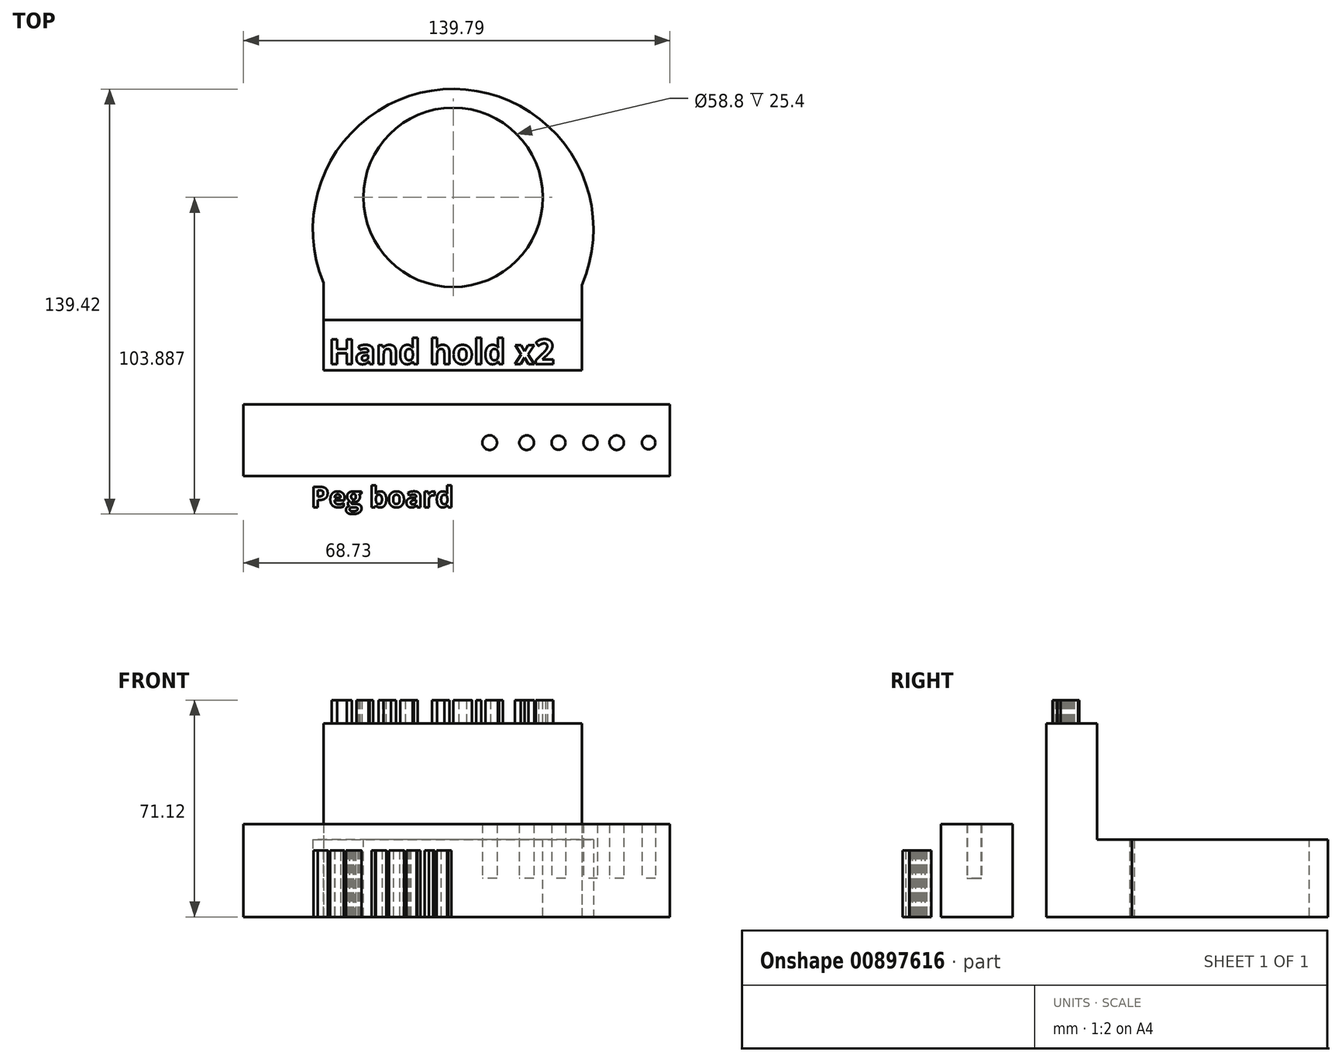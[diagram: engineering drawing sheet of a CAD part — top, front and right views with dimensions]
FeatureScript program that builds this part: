
annotation { "Feature Type Name" : "Feature", "Feature Type Description" : "" }
export const myFeature = defineFeature(function(context is Context, id is Id, definition is map)
    precondition{}
    {
        {
            var Q0;
            Q0=makeQuery(id+"FttHBKo60JJalxO_0.opExtrude","CAP_FACE",FACE,{"disambiguationData":[OSD([sQuery(id+"FFDxyAQckOqJVPz_0.wireOp",EDGE,"cAa8GNnS-9NBn-fBWv-4bFi-mSQCbdk5DH3K"),sQuery(id+"FFDxyAQckOqJVPz_0.wireOp",EDGE,"T3loh2Vf-emFG-5iRX-t4Wo-vKlrmD9mAp1y.bottom"),sQuery(id+"FFDxyAQckOqJVPz_0.wireOp",EDGE,"T3loh2Vf-emFG-5iRX-t4Wo-vKlrmD9mAp1y.top"),sQuery(id+"FFDxyAQckOqJVPz_0.wireOp",EDGE,"T3loh2Vf-emFG-5iRX-t4Wo-vKlrmD9mAp1y.left"),sQuery(id+"FFDxyAQckOqJVPz_0.wireOp",EDGE,"T3loh2Vf-emFG-5iRX-t4Wo-vKlrmD9mAp1y.right"),sQuery(id+"FFDxyAQckOqJVPz_0.wireOp",EDGE,"rmxbEG8E-x7te-680N-vgeH-4cutX0Q7IRPg")])],"isStart":false});
            var sketch = newSketch(context, id + "F0", { "sketchPlane" : qUnion([Q0])});
            skLineSegment(sketch, "E0.bottom", {"start": v(-58.06, -65.24) * mm, "end": v(58.26, -65.24) * mm});
            skLineSegment(sketch, "E0.top", {"start": v(-58.06, -53.15) * mm, "end": v(58.26, -53.15) * mm});
            skLineSegment(sketch, "E0.left", {"start": v(-58.06, -65.24) * mm, "end": v(-58.06, -53.15) * mm});
            skLineSegment(sketch, "E0.right", {"start": v(58.26, -65.24) * mm, "end": v(58.26, -53.15) * mm});
            skSolve(sketch);
        }
        {
            var Q0;
            Q0=qCreatedBy(makeId("Top.planeOp"),FACE);
            var sketch = newSketch(context, id + "F1", { "sketchPlane" : qUnion([Q0])});
            skCircle(sketch, "E1", {"center": v(0, 17.56) * mm, "radius": 46 * mm});
            skLineSegment(sketch, "E2.bottom", {"start": v(-42.51, 0) * mm, "end": v(42.21, 0) * mm});
            skLineSegment(sketch, "E2.top", {"start": v(-42.51, -28.72) * mm, "end": v(42.21, -28.72) * mm});
            skLineSegment(sketch, "E2.left", {"start": v(-42.51, 0) * mm, "end": v(-42.51, -28.72) * mm});
            skLineSegment(sketch, "E2.right", {"start": v(42.21, 0) * mm, "end": v(42.21, -28.72) * mm});
            skSolve(sketch);
        }
        {
            var Q0;
            {var subQ0=sQuery(id+"F1.wireOp",EDGE,"E2.bottom");Q0=makeQuery(id+"F1.imprint","IMPRINT",FACE,{"disambiguationData":[TD([[makeQuery(id+"F1.imprint","IMPRINT",EDGE,{"derivedFrom":subQ0}),1.0]])]});}
            var Q1;
            {var subQ0=sQuery(id+"F1.wireOp",EDGE,"E2.bottom");Q1=makeQuery(id+"F1.imprint","IMPRINT",FACE,{"disambiguationData":[TD([[makeQuery(id+"F1.imprint","IMPRINT",EDGE,{"derivedFrom":subQ0}),-1.0]])]});}
            var Q2;
            {var subQ4=sQuery(id+"F1.wireOp",EDGE,"E2.top");Q2=makeQuery(id+"F1.imprint","IMPRINT",FACE,{"disambiguationData":[TD([[makeQuery(id+"F1.imprint","IMPRINT",EDGE,{"derivedFrom":subQ4}),1.0]])]});}
            extrude(context, id + "F2", {"entities" : qUnion([Q0, Q1, Q2]), "depth" : 25.4 * mm, "offsetDistance" : 25.4 * mm});
        }
        {
            var Q0;
            Q0=makeQuery(id+"F2.opExtrude","CAP_FACE",FACE,{"disambiguationData":[OSD([sQuery(id+"F1.wireOp",EDGE,"E1"),sQuery(id+"F1.wireOp",EDGE,"E2.top"),sQuery(id+"F1.wireOp",EDGE,"E2.left"),sQuery(id+"F1.wireOp",EDGE,"E2.right")])],"isStart":false});
            var sketch = newSketch(context, id + "F3", { "sketchPlane" : qUnion([Q0])});
            skCircle(sketch, "E3", {"center": v(0, 28.03) * mm, "radius": 29.4 * mm});
            skSolve(sketch);
        }
        {
            var Q0;
            Q0=makeQuery(id+"F3.imprint","IMPRINT",FACE,{"disambiguationData":[TD([[makeQuery(id+"F3.imprint","IMPRINT",EDGE,{"derivedFrom":sQuery(id+"F3.wireOp",EDGE,"E3")}),1.0]])]});
            extrude(context, id + "F4", {"entities" : qUnion([Q0]), "operationType" : NewBodyOperationType.REMOVE, "oppositeDirection" : true, "depth" : 56.13 * mm, "offsetDistance" : 25.4 * mm});
        }
        {
            var Q0;
            Q0=makeQuery(id+"F2.opExtrude","CAP_FACE",FACE,{"disambiguationData":[OSD([sQuery(id+"F1.wireOp",EDGE,"E1"),sQuery(id+"F1.wireOp",EDGE,"E2.top"),sQuery(id+"F1.wireOp",EDGE,"E2.left"),sQuery(id+"F1.wireOp",EDGE,"E2.right")])],"isStart":false});
            var sketch = newSketch(context, id + "F5", { "sketchPlane" : qUnion([Q0])});
            skLineSegment(sketch, "E4.bottom", {"start": v(-42.51, -28.72) * mm, "end": v(42.21, -28.72) * mm});
            skLineSegment(sketch, "E4.top", {"start": v(-42.51, -12.21) * mm, "end": v(42.21, -12.21) * mm});
            skLineSegment(sketch, "E4.left", {"start": v(-42.51, -28.72) * mm, "end": v(-42.51, -12.21) * mm});
            skLineSegment(sketch, "E4.right", {"start": v(42.21, -28.72) * mm, "end": v(42.21, -12.21) * mm});
            skSolve(sketch);
        }
        {
            var Q0;
            Q0=makeQuery(id+"F5.imprint","IMPRINT",FACE,{"disambiguationData":[TD([[makeQuery(id+"F5.imprint","IMPRINT",EDGE,{"derivedFrom":sQuery(id+"F5.wireOp",EDGE,"E4.bottom")}),1.0]])]});
            extrude(context, id + "F6", {"entities" : qUnion([Q0]), "operationType" : NewBodyOperationType.ADD, "depth" : 38.1 * mm, "offsetDistance" : 25.4 * mm});
        }
        {
            var Q0;
            Q0=qCreatedBy(makeId("Top.planeOp"),FACE);
            var sketch = newSketch(context, id + "F7", { "sketchPlane" : qUnion([Q0])});
            skLineSegment(sketch, "E5.bottom", {"start": v(-68.73, -39.89) * mm, "end": v(71.06, -39.89) * mm});
            skLineSegment(sketch, "E5.top", {"start": v(-68.73, -63.38) * mm, "end": v(71.06, -63.38) * mm});
            skLineSegment(sketch, "E5.left", {"start": v(-68.73, -39.89) * mm, "end": v(-68.73, -63.38) * mm});
            skLineSegment(sketch, "E5.right", {"start": v(71.06, -39.89) * mm, "end": v(71.06, -63.38) * mm});
            skSolve(sketch);
        }
        {
            var Q0;
            Q0=makeQuery(id+"F7.imprint","IMPRINT",FACE,{"disambiguationData":[TD([[makeQuery(id+"F7.imprint","IMPRINT",EDGE,{"derivedFrom":sQuery(id+"F7.wireOp",EDGE,"E5.bottom")}),-1.0]])]});
            extrude(context, id + "F8", {"entities" : qUnion([Q0]), "depth" : 12.7 * mm, "offsetDistance" : 25.4 * mm});
        }
        {
            var Q0;
            Q0=makeQuery(id+"F8.opExtrude","CAP_FACE",FACE,{"disambiguationData":[OSD([sQuery(id+"F7.wireOp",EDGE,"E5.bottom"),sQuery(id+"F7.wireOp",EDGE,"E5.top"),sQuery(id+"F7.wireOp",EDGE,"E5.left"),sQuery(id+"F7.wireOp",EDGE,"E5.right")])],"isStart":false});
            var sketch = newSketch(context, id + "F9", { "sketchPlane" : qUnion([Q0])});
            skCircle(sketch, "E6", {"center": v(0, -52.45) * mm, "radius": 2.42 * mm});
            skCircle(sketch, "E7", {"center": v(-11.98, -52.45) * mm, "radius": 2.4 * mm});
            skCircle(sketch, "E8", {"center": v(-24.07, -52.45) * mm, "radius": 2.4 * mm});
            skCircle(sketch, "E9", {"center": v(-34.54, -52.45) * mm, "radius": 2.3 * mm});
            skCircle(sketch, "E10", {"center": v(-45, -52.45) * mm, "radius": 2.3 * mm});
            skCircle(sketch, "E11", {"center": v(-53.61, -52.45) * mm, "radius": 2.37 * mm});
            skCircle(sketch, "E12", {"center": v(-64.08, -52.45) * mm, "radius": 2.2 * mm});
            skCircle(sketch, "E13.MirrorC", {"center": v(64.08, -52.45) * mm, "radius": 2.2 * mm});
            skCircle(sketch, "E14.MirrorC", {"center": v(53.61, -52.45) * mm, "radius": 2.37 * mm});
            skCircle(sketch, "E15.MirrorC", {"center": v(45, -52.45) * mm, "radius": 2.3 * mm});
            skCircle(sketch, "E16.MirrorC", {"center": v(34.54, -52.45) * mm, "radius": 2.3 * mm});
            skCircle(sketch, "E17.MirrorC", {"center": v(24.07, -52.45) * mm, "radius": 2.4 * mm});
            skCircle(sketch, "E18.MirrorC", {"center": v(11.98, -52.45) * mm, "radius": 2.4 * mm});
            skSolve(sketch);
        }
        {
            var Q0;
            Q0=makeQuery(id+"F9.imprint","IMPRINT",FACE,{"disambiguationData":[TD([[makeQuery(id+"F9.imprint","IMPRINT",EDGE,{"derivedFrom":sQuery(id+"F9.wireOp",EDGE,"E12")}),1.0]])]});
            var Q1;
            Q1=makeQuery(id+"F9.imprint","IMPRINT",FACE,{"disambiguationData":[TD([[makeQuery(id+"F9.imprint","IMPRINT",EDGE,{"derivedFrom":sQuery(id+"F9.wireOp",EDGE,"E11")}),1.0]])]});
            var Q2;
            Q2=makeQuery(id+"F9.imprint","IMPRINT",FACE,{"disambiguationData":[TD([[makeQuery(id+"F9.imprint","IMPRINT",EDGE,{"derivedFrom":sQuery(id+"F9.wireOp",EDGE,"E10")}),1.0]])]});
            var Q3;
            Q3=makeQuery(id+"F9.imprint","IMPRINT",FACE,{"disambiguationData":[TD([[makeQuery(id+"F9.imprint","IMPRINT",EDGE,{"derivedFrom":sQuery(id+"F9.wireOp",EDGE,"E9")}),1.0]])]});
            var Q4;
            Q4=makeQuery(id+"F9.imprint","IMPRINT",FACE,{"disambiguationData":[TD([[makeQuery(id+"F9.imprint","IMPRINT",EDGE,{"derivedFrom":sQuery(id+"F9.wireOp",EDGE,"E8")}),1.0]])]});
            var Q5;
            Q5=makeQuery(id+"F9.imprint","IMPRINT",FACE,{"disambiguationData":[TD([[makeQuery(id+"F9.imprint","IMPRINT",EDGE,{"derivedFrom":sQuery(id+"F9.wireOp",EDGE,"E6")}),1.0]])]});
            var Q6;
            Q6=makeQuery(id+"F9.imprint","IMPRINT",FACE,{"disambiguationData":[TD([[makeQuery(id+"F9.imprint","IMPRINT",EDGE,{"derivedFrom":sQuery(id+"F9.wireOp",EDGE,"E7")}),1.0]])]});
            var Q7;
            Q7=makeQuery(id+"F9.imprint","IMPRINT",FACE,{"disambiguationData":[TD([[makeQuery(id+"F9.imprint","IMPRINT",EDGE,{"derivedFrom":sQuery(id+"F9.wireOp",EDGE,"E18.MirrorC")}),-1.0]])]});
            var Q8;
            Q8=makeQuery(id+"F9.imprint","IMPRINT",FACE,{"disambiguationData":[TD([[makeQuery(id+"F9.imprint","IMPRINT",EDGE,{"derivedFrom":sQuery(id+"F9.wireOp",EDGE,"E17.MirrorC")}),-1.0]])]});
            var Q9;
            Q9=makeQuery(id+"F9.imprint","IMPRINT",FACE,{"disambiguationData":[TD([[makeQuery(id+"F9.imprint","IMPRINT",EDGE,{"derivedFrom":sQuery(id+"F9.wireOp",EDGE,"E16.MirrorC")}),-1.0]])]});
            var Q10;
            Q10=makeQuery(id+"F9.imprint","IMPRINT",FACE,{"disambiguationData":[TD([[makeQuery(id+"F9.imprint","IMPRINT",EDGE,{"derivedFrom":sQuery(id+"F9.wireOp",EDGE,"E15.MirrorC")}),-1.0]])]});
            var Q11;
            Q11=makeQuery(id+"F9.imprint","IMPRINT",FACE,{"disambiguationData":[TD([[makeQuery(id+"F9.imprint","IMPRINT",EDGE,{"derivedFrom":sQuery(id+"F9.wireOp",EDGE,"E14.MirrorC")}),-1.0]])]});
            var Q12;
            Q12=makeQuery(id+"F9.imprint","IMPRINT",FACE,{"disambiguationData":[TD([[makeQuery(id+"F9.imprint","IMPRINT",EDGE,{"derivedFrom":sQuery(id+"F9.wireOp",EDGE,"E13.MirrorC")}),-1.0]])]});
            extrude(context, id + "F10", {"entities" : qUnion([Q0, Q1, Q2, Q3, Q4, Q5, Q6, Q7, Q8, Q9, Q10, Q11, Q12]), "operationType" : NewBodyOperationType.ADD, "depth" : 17.78 * mm, "offsetDistance" : 25.4 * mm});
        }
        {
            var Q0;
            Q0=makeQuery(id+"F6.opExtrude","CAP_FACE",FACE,{"disambiguationData":[OSD([sQuery(id+"F5.wireOp",EDGE,"E4.bottom"),sQuery(id+"F5.wireOp",EDGE,"E4.top"),sQuery(id+"F5.wireOp",EDGE,"E4.left"),sQuery(id+"F5.wireOp",EDGE,"E4.right")])],"isStart":false});
            var sketch = newSketch(context, id + "F11", { "sketchPlane" : qUnion([Q0])});
            skText(sketch, "E19", { "text": "Hand hold x2", "fontName": "OpenSans-Bold.ttf"});
            const initialGuessF11  = {"E19": [-0.04082, -0.02663, 1, 0, 0.00814]};
            skSetInitialGuess(sketch, initialGuessF11);
            skSolve(sketch);
        }
        {
            var Q0;
            Q0 = qSketchRegion(id + "F11", true);
            extrude(context, id + "F12", {"entities" : qUnion([Q0]), "operationType" : NewBodyOperationType.ADD, "depth" : 7.62 * mm, "offsetDistance" : 25.4 * mm});
        }
        {
            var Q0;
            Q0=qCreatedBy(makeId("Top.planeOp"),FACE);
            var sketch = newSketch(context, id + "F13", { "sketchPlane" : qUnion([Q0])});
            skText(sketch, "E20", { "text": "Peg board", "fontName": "OpenSans-Bold.ttf"});
            const initialGuessF13  = {"E20": [-0.0466, -0.07361, 1, 0, 0.00675]};
            skSetInitialGuess(sketch, initialGuessF13);
            skSolve(sketch);
        }
        {
            var Q0;
            Q0 = qSketchRegion(id + "F13", true);
            extrude(context, id + "F14", {"entities" : qUnion([Q0]), "depth" : 21.84 * mm, "offsetDistance" : 25.4 * mm});
        }
    });
